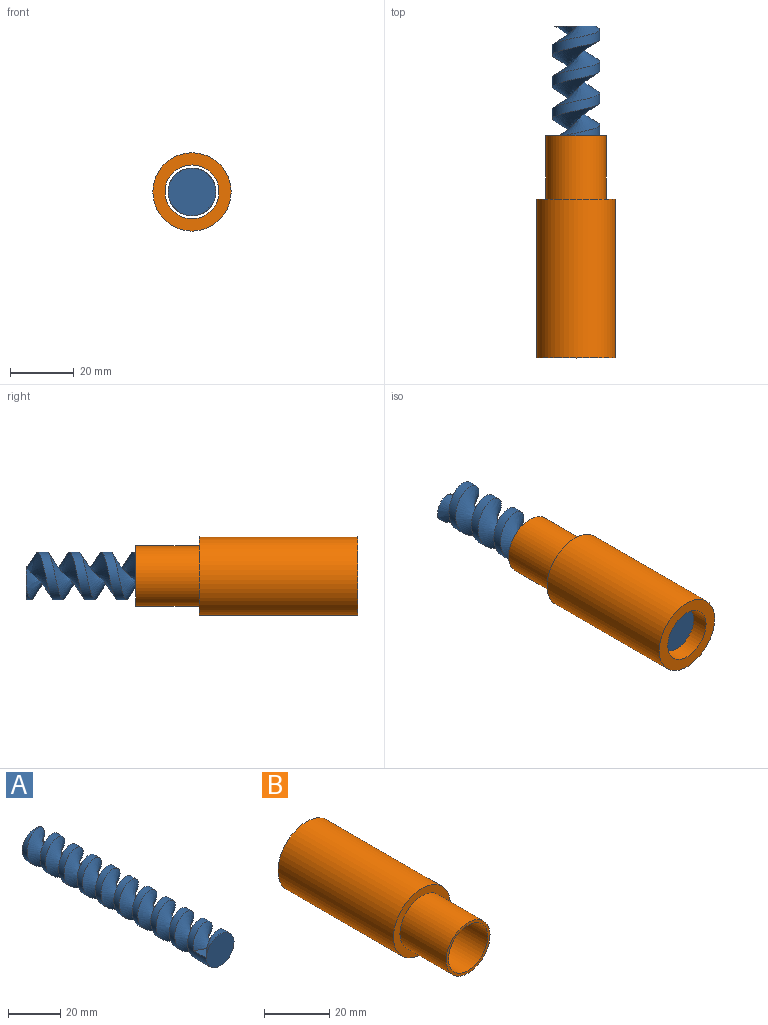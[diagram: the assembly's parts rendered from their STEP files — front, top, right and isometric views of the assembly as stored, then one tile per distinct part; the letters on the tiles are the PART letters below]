
ASSEMBLY  parts=2 mates=1
PART A: 6 faces, bbox 15x104.5x15 mm
  f0: cylinder r=7.5mm len=100mm, axis (0,1,0), area 1924.9mm2, adj f1,f2,f3,f4,f5
  f1: plane 15x15mm, normal (0,-1,0), area 176.7mm2, adj f0
  f2: plane 12.26x11.51mm, normal (0,1,0), area 103.7mm2, adj f0,f3,f4
  f3: bspline ~103.5x15mm, area 2049.2mm2, adj f0,f2,f4,f5
  f4: bspline ~101x15mm, area 1956.7mm2, adj f0,f2,f3,f5
  f5: plane 7x6.06mm, normal (0,0,1), area 21.2mm2, adj f0,f3,f4
PART B: 6 faces, bbox 24.6x70x24.6 mm
  f0: cylinder r=8.5mm len=70mm, axis (0,1,0), area 3738.5mm2, adj f2,f4
  f1: cylinder r=9.5mm len=20mm, axis (0,1,0), area 1193.8mm2, adj f2,f5
  f2: plane 19x19mm, normal (0,-1,0), area 56.5mm2, adj f0,f1
  f3: cylinder r=12.32mm len=50mm, axis (0,-1,0), area 3870.2mm2, adj f4,f5
  f4: plane 24.64x24.64mm, normal (0,1,0), area 249.8mm2, adj f0,f3
  f5: plane 24.64x24.64mm, normal (0,-1,0), area 193.3mm2, adj f1,f3
PLACE A rot(axis=(0,-1,0),137.3deg) t=(-37.61,-19.42,63.89)mm
PLACE B rot(axis=(1,0,0),180deg) t=(-37.87,-73.95,63.61)mm
MATE cylindrical B.f0 <-> A.f0  axis (0,1,0) through (-37.87,-53.95,63.61)mm
